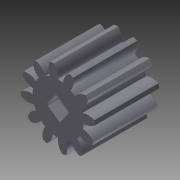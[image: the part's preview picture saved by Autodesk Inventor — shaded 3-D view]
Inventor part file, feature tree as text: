
AUTODESK INVENTOR PART (.ipt)
format: ipt  version: 2013 (Build 170138000, 138)  size: 167,936 bytes
history: native  units: in
note: dims shown in document units (in); Inventor stores cm internally (conversion verified against a paired STEP export)
features: extrude x2, sketch x2, other x1
ambient origin geometry x8: Origin, YZ Plane, XZ Plane, XY Plane, X Axis, Y Axis, Z Axis, Center Point
bodies: Solid1 (feature_tree)
feature tree (5):
  extrude  "Extrusion1"  Depth=1.0in TaperAngle=0.0deg
  sketch  "Sketch1"  dims[d0=0.5in d1=0.0in d2=1.0in d3=0.0in]
  sketch  "Sketch2"  dims[d4=0.0in d5=0.0in]
  other  "Srf1"
  extrude  "ExtrusionSrf1"  TaperAngle=0.0deg  [1 undecoded]
note: 1 required parameter value undecoded (feature->parameter linkage not recoverable at this tier; creation-order binding heuristic only, values carry confidence <= 0.55)
